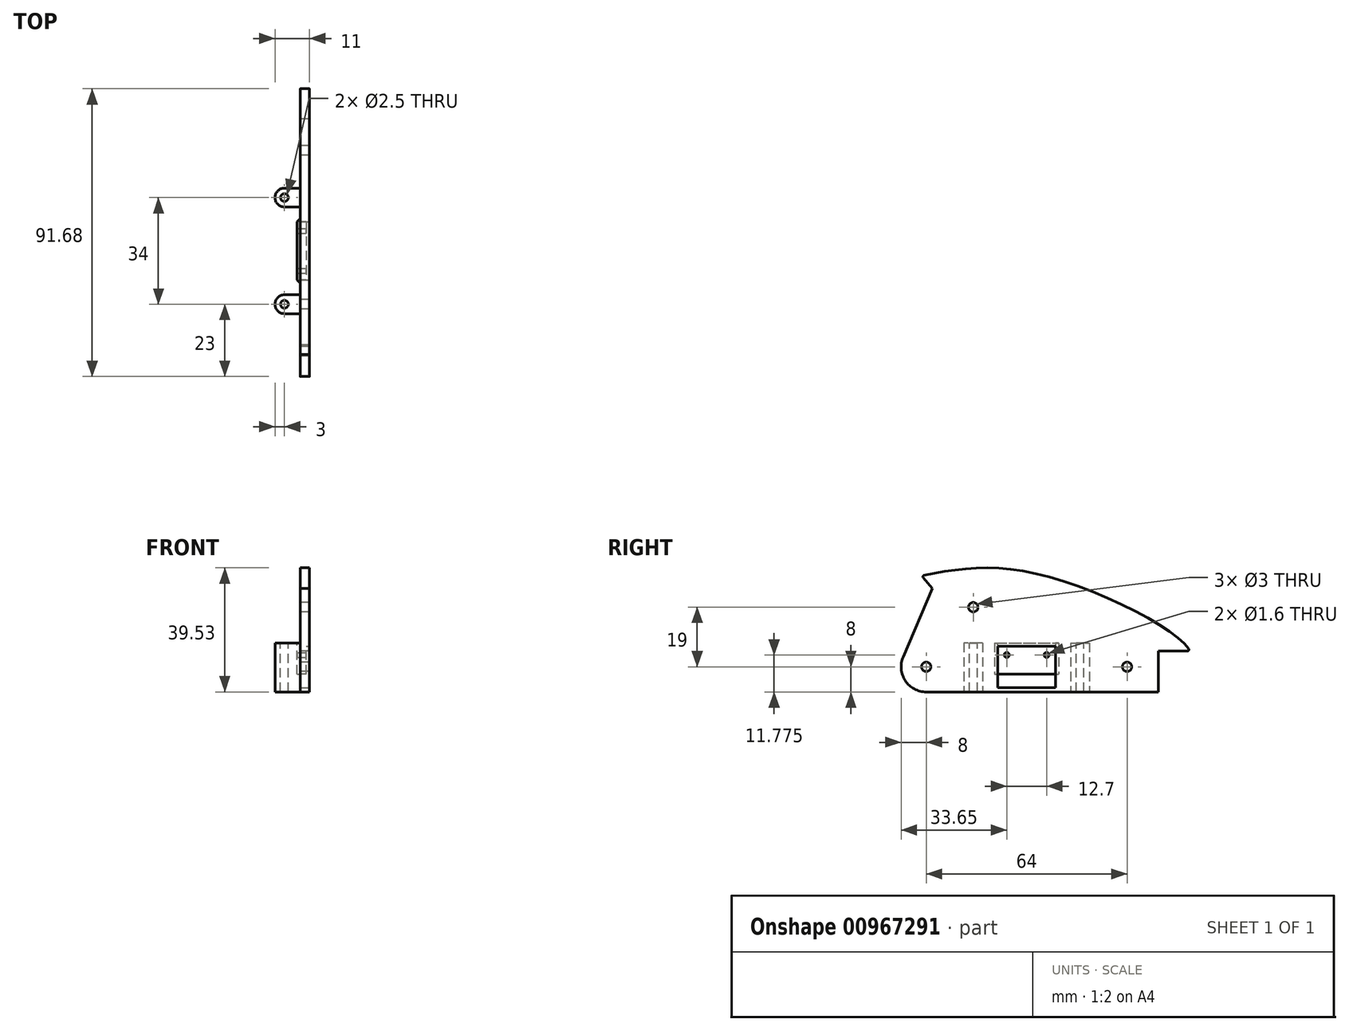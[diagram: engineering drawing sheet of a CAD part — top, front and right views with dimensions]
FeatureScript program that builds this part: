
annotation { "Feature Type Name" : "Feature", "Feature Type Description" : "" }
export const myFeature = defineFeature(function(context is Context, id is Id, definition is map)
    precondition{}
    {
        {
            var Q0;
            Q0=qCreatedBy(makeId("Right.planeOp"),FACE);
            var sketch = newSketch(context, id + "F0", { "sketchPlane" : qUnion([Q0])});
            skCircle(sketch, "E0", {"center": v(0, 0) * mm, "radius": 1.5 * mm});
            skCircle(sketch, "E1", {"center": v(-64, 0) * mm, "radius": 1.5 * mm});
            skCircle(sketch, "E2", {"center": v(-49, 19) * mm, "radius": 1.5 * mm});
            skLineSegment(sketch, "E3", {"start": v(10, -8) * mm, "end": v(-64, -8) * mm});
            skPoint(sketch, "E4", {"position": v(-62, 25) * mm});
            skPoint(sketch, "E5", {"position": v(-65.5, 29) * mm});
            skLineSegment(sketch, "E6", {"start": v(-62, 25) * mm, "end": v(-65.5, 29) * mm});
            skLineSegment(sketch, "E7", {"start": v(10, -8) * mm, "end": v(10, 5) * mm});
            skLineSegment(sketch, "E8", {"start": v(10, 5) * mm, "end": v(20, 5) * mm});
            skFitSpline(sketch, "E9", {"points": [v(-65.5, 29) * mm, v(-25.03, 28.72) * mm, v(20, 5) * mm], "startDerivative": vector(78.35, 16.4) * mm, "endDerivative": vector(13.23, -33.9) * mm});
            skArc(sketch, "E10", {"start": v(-64, -8) * mm, "mid": v(-70.68, -4.4) * mm, "end": v(-71.35, 3.15) * mm});
            skLineSegment(sketch, "E11", {"start": v(-71.35, 3.15) * mm, "end": v(-62, 25) * mm});
            skSolve(sketch);
        }
        {
            var Q0;
            Q0=makeQuery(id+"F0.imprint","IMPRINT",FACE,{"disambiguationData":[TD([[makeQuery(id+"F0.imprint","IMPRINT",EDGE,{"derivedFrom":sQuery(id+"F0.wireOp",EDGE,"E0")}),-1.0]])]});
            extrude(context, id + "F1", {"entities" : qUnion([Q0]), "depth" : 3 * mm, "offsetDistance" : 25 * mm});
        }
        {
            var Q0;
            Q0=makeQuery(id+"F1.opExtrude","CAP_FACE",FACE,{"disambiguationData":[OSD([sQuery(id+"F0.wireOp",EDGE,"E0"),sQuery(id+"F0.wireOp",EDGE,"E1"),sQuery(id+"F0.wireOp",EDGE,"E2"),sQuery(id+"F0.wireOp",EDGE,"E3"),sQuery(id+"F0.wireOp",EDGE,"E6"),sQuery(id+"F0.wireOp",EDGE,"E7"),sQuery(id+"F0.wireOp",EDGE,"E8"),sQuery(id+"F0.wireOp",EDGE,"E9"),sQuery(id+"F0.wireOp",EDGE,"E10"),sQuery(id+"F0.wireOp",EDGE,"E11")])],"isStart":false});
            var sketch = newSketch(context, id + "F2", { "sketchPlane" : qUnion([Q0])});
            skLineSegment(sketch, "E12", {"start": v(-64, 0) * mm, "end": v(0, 0) * mm});
            skLineSegment(sketch, "E13.bottom", {"start": v(-22.75, -6.63) * mm, "end": v(-41.25, -6.63) * mm});
            skLineSegment(sketch, "E13.top", {"start": v(-22.75, 6.62) * mm, "end": v(-41.25, 6.63) * mm});
            skLineSegment(sketch, "E13.left", {"start": v(-22.75, -6.63) * mm, "end": v(-22.75, 6.62) * mm});
            skLineSegment(sketch, "E13.right", {"start": v(-41.25, -6.63) * mm, "end": v(-41.25, 6.63) * mm});
            skPoint(sketch, "E13.middle", {"position": v(-32, 0) * mm});
            skSolve(sketch);
        }
        {
            var Q0;
            {var subQ5=sQuery(id+"F2.wireOp",EDGE,"E13.top");Q0=makeQuery(id+"F2.imprint","IMPRINT",FACE,{"disambiguationData":[TD([[makeQuery(id+"F2.imprint","IMPRINT",EDGE,{"derivedFrom":subQ5}),1.0]])]});}
            var Q1;
            {var subQ5=sQuery(id+"F2.wireOp",EDGE,"E13.bottom");Q1=makeQuery(id+"F2.imprint","IMPRINT",FACE,{"disambiguationData":[TD([[makeQuery(id+"F2.imprint","IMPRINT",EDGE,{"derivedFrom":subQ5}),-1.0]])]});}
            extrude(context, id + "F3", {"entities" : qUnion([Q0, Q1]), "operationType" : NewBodyOperationType.REMOVE, "oppositeDirection" : true, "depth" : 25 * mm, "offsetDistance" : 25 * mm});
        }
        {
            var Q0;
            Q0=makeQuery(id+"F1.opExtrude","CAP_FACE",FACE,{"disambiguationData":[OSD([sQuery(id+"F0.wireOp",EDGE,"E0"),sQuery(id+"F0.wireOp",EDGE,"E1"),sQuery(id+"F0.wireOp",EDGE,"E2"),sQuery(id+"F0.wireOp",EDGE,"E3"),sQuery(id+"F0.wireOp",EDGE,"E6"),sQuery(id+"F0.wireOp",EDGE,"E7"),sQuery(id+"F0.wireOp",EDGE,"E8"),sQuery(id+"F0.wireOp",EDGE,"E9"),sQuery(id+"F0.wireOp",EDGE,"E10"),sQuery(id+"F0.wireOp",EDGE,"E11")])],"isStart":true});
            var sketch = newSketch(context, id + "F4", { "sketchPlane" : qUnion([Q0])});
            skLineSegment(sketch, "E14.bottom", {"start": v(42.25, 7.63) * mm, "end": v(21.75, 7.62) * mm});
            skLineSegment(sketch, "E14.top", {"start": v(42.25, -2.37) * mm, "end": v(21.75, -2.38) * mm});
            skLineSegment(sketch, "E14.left", {"start": v(42.25, 7.63) * mm, "end": v(42.25, -2.37) * mm});
            skLineSegment(sketch, "E14.right", {"start": v(21.75, 7.62) * mm, "end": v(21.75, -2.38) * mm});
            skPoint(sketch, "E14.middle", {"position": v(32, 2.63) * mm});
            skPoint(sketch, "E14.middle.positionSnap0", {"position": v(32, 6.63) * mm});
            skPoint(sketch, "E14.centerSnap0", {"position": v(32, 6.63) * mm});
            skSolve(sketch);
        }
        {
            var Q0;
            {var subQ1=makeQuery(id+"F1.opExtrude","CAP_FACE",FACE,{"disambiguationData":[OSD([sQuery(id+"F0.wireOp",EDGE,"E0"),sQuery(id+"F0.wireOp",EDGE,"E1"),sQuery(id+"F0.wireOp",EDGE,"E2"),sQuery(id+"F0.wireOp",EDGE,"E3"),sQuery(id+"F0.wireOp",EDGE,"E6"),sQuery(id+"F0.wireOp",EDGE,"E7"),sQuery(id+"F0.wireOp",EDGE,"E8"),sQuery(id+"F0.wireOp",EDGE,"E9"),sQuery(id+"F0.wireOp",EDGE,"E10"),sQuery(id+"F0.wireOp",EDGE,"E11")])],"isStart":true});var subQ6=makeQuery(id+"F3.boolean.opBoolean","INTERSECT",EDGE,{"derivedFrom":[subQ1,makeQuery(id+"F3.opExtrude","SWEPT_FACE",FACE,{"disambiguationData":[OSD([sQuery(id+"F2.wireOp",EDGE,"E13.top")])]})]});Q0=makeQuery(id+"F4.imprint","IMPRINT",FACE,{"disambiguationData":[TD([[makeQuery(id+"F4.imprint","IMPRINT",EDGE,{"derivedFrom":subQ6}),-1.0]])]});}
            var Q1;
            Q1=makeQuery(id+"F4.imprint","IMPRINT",FACE,{"disambiguationData":[TD([[makeQuery(id+"F4.imprint","IMPRINT",EDGE,{"derivedFrom":sQuery(id+"F4.wireOp",EDGE,"E14.bottom")}),1.0]])]});
            extrude(context, id + "F5", {"entities" : qUnion([Q0, Q1]), "operationType" : NewBodyOperationType.ADD, "depth" : 1 * mm, "offsetDistance" : 25 * mm});
        }
        {
            var Q0;
            Q0=makeQuery(id+"F5.opExtrude","CAP_FACE",FACE,{"disambiguationData":[OSD([sQuery(id+"F4.wireOp",EDGE,"E14.bottom"),sQuery(id+"F4.wireOp",EDGE,"E14.top"),sQuery(id+"F4.wireOp",EDGE,"E14.left"),sQuery(id+"F4.wireOp",EDGE,"E14.right")])],"isStart":true});
            extrude(context, id + "F6", {"entities" : qUnion([Q0]), "operationType" : NewBodyOperationType.ADD, "depth" : 2 * mm, "offsetDistance" : 25 * mm});
        }
        {
            var Q0;
            Q0=makeQuery(id+"F6.opExtrude","CAP_FACE",FACE,{"disambiguationData":[OSD([sQuery(id+"F4.wireOp",EDGE,"E14.bottom"),sQuery(id+"F4.wireOp",EDGE,"E14.top"),sQuery(id+"F4.wireOp",EDGE,"E14.left"),sQuery(id+"F4.wireOp",EDGE,"E14.right")])],"isStart":false});
            var sketch = newSketch(context, id + "F7", { "sketchPlane" : qUnion([Q0])});
            skPoint(sketch, "E15", {"position": v(-32, 3.78) * mm});
            skPoint(sketch, "E15.positionSnap0", {"position": v(-32, 6.63) * mm});
            skPoint(sketch, "E16", {"position": v(-38.35, 3.78) * mm});
            skPoint(sketch, "E17", {"position": v(-25.65, 3.78) * mm});
            skSolve(sketch);
        }
        {
            var Q0;
            Q0=sQuery(id+"F7.wireOp",VERTEX,"E16");
            var Q1;
            Q1=sQuery(id+"F7.wireOp",VERTEX,"E17");
            var Q2;
            Q2=makeQuery(id+"F1.opExtrude","SWEPT_BODY",BODY,{"disambiguationData":[OSD([sQuery(id+"F0.wireOp",EDGE,"E0"),sQuery(id+"F0.wireOp",EDGE,"E1"),sQuery(id+"F0.wireOp",EDGE,"E2"),sQuery(id+"F0.wireOp",EDGE,"E3"),sQuery(id+"F0.wireOp",EDGE,"E6"),sQuery(id+"F0.wireOp",EDGE,"E7"),sQuery(id+"F0.wireOp",EDGE,"E8"),sQuery(id+"F0.wireOp",EDGE,"E9"),sQuery(id+"F0.wireOp",EDGE,"E10"),sQuery(id+"F0.wireOp",EDGE,"E11")])]});
            hole(context, id + "F8", {"style" : HoleStyle.SIMPLE, "endStyle" : HoleEndStyle.THROUGH, "holeDiameter" : 1.6 * mm, "majorDiameter" : 5 * mm, "tappedDepth" : 12 * mm, "tapClearance" : 3, "startFromSketch" : true, "locations" : qUnion([Q0, Q1]), "scope" : qUnion([Q2])});
        }
        {
            var Q0;
            Q0=makeQuery(id+"F5.opExtrude","CAP_EDGE",EDGE,{"disambiguationData":[OSD([sQuery(id+"F4.wireOp",EDGE,"E14.right")])],"isStart":false});
            var Q1;
            Q1=makeQuery(id+"F5.opExtrude","CAP_EDGE",EDGE,{"disambiguationData":[OSD([sQuery(id+"F4.wireOp",EDGE,"E14.left")])],"isStart":false});
            chamfer(context, id + "F9", {"entities" : qUnion([Q0, Q1]), "width" : 1 * mm, "tangentPropagation" : true});
        }
        {
            var Q0;
            Q0=makeQuery(id+"F1.opExtrude","CAP_FACE",FACE,{"disambiguationData":[OSD([sQuery(id+"F0.wireOp",EDGE,"E0"),sQuery(id+"F0.wireOp",EDGE,"E1"),sQuery(id+"F0.wireOp",EDGE,"E2"),sQuery(id+"F0.wireOp",EDGE,"E3"),sQuery(id+"F0.wireOp",EDGE,"E6"),sQuery(id+"F0.wireOp",EDGE,"E7"),sQuery(id+"F0.wireOp",EDGE,"E8"),sQuery(id+"F0.wireOp",EDGE,"E9"),sQuery(id+"F0.wireOp",EDGE,"E10"),sQuery(id+"F0.wireOp",EDGE,"E11")])],"isStart":true});
            var sketch = newSketch(context, id + "F10", { "sketchPlane" : qUnion([Q0])});
            skPoint(sketch, "E18", {"position": v(49, 19) * mm});
            skLineSegment(sketch, "E19.bottom", {"start": v(46, 7.63) * mm, "end": v(52, 7.63) * mm});
            skLineSegment(sketch, "E19.top", {"start": v(46, 1.63) * mm, "end": v(52, 1.63) * mm});
            skLineSegment(sketch, "E19.left", {"start": v(46, 7.63) * mm, "end": v(46, 1.63) * mm});
            skLineSegment(sketch, "E19.right", {"start": v(52, 7.63) * mm, "end": v(52, 1.63) * mm});
            skPoint(sketch, "E19.middle", {"position": v(49, 4.63) * mm});
            skSolve(sketch);
        }
        {
            var Q0;
            Q0=makeQuery(id+"F10.imprint","IMPRINT",FACE,{"disambiguationData":[TD([[makeQuery(id+"F10.imprint","IMPRINT",EDGE,{"derivedFrom":sQuery(id+"F10.wireOp",EDGE,"E19.bottom")}),-1.0]])]});
            extrude(context, id + "F11", {"entities" : qUnion([Q0]), "operationType" : NewBodyOperationType.ADD, "depth" : 8 * mm, "offsetDistance" : 25 * mm});
        }
        {
            var Q0;
            Q0=makeQuery(id+"F11.opExtrude","CAP_EDGE",EDGE,{"disambiguationData":[OSD([sQuery(id+"F10.wireOp",EDGE,"E19.right")])],"isStart":false});
            var Q1;
            Q1=makeQuery(id+"F11.opExtrude","CAP_EDGE",EDGE,{"disambiguationData":[OSD([sQuery(id+"F10.wireOp",EDGE,"E19.left")])],"isStart":false});
            fillet(context, id + "F12", {"entities" : qUnion([Q0, Q1]), "radius" : 3 * mm, "tangentPropagation" : true, "allowEdgeOverflow" : false});
        }
        {
            var Q0;
            Q0=makeQuery(id+"F1.opExtrude","CAP_FACE",FACE,{"disambiguationData":[OSD([sQuery(id+"F0.wireOp",EDGE,"E0"),sQuery(id+"F0.wireOp",EDGE,"E1"),sQuery(id+"F0.wireOp",EDGE,"E2"),sQuery(id+"F0.wireOp",EDGE,"E3"),sQuery(id+"F0.wireOp",EDGE,"E6"),sQuery(id+"F0.wireOp",EDGE,"E7"),sQuery(id+"F0.wireOp",EDGE,"E8"),sQuery(id+"F0.wireOp",EDGE,"E9"),sQuery(id+"F0.wireOp",EDGE,"E10"),sQuery(id+"F0.wireOp",EDGE,"E11")])],"isStart":true});
            var sketch = newSketch(context, id + "F13", { "sketchPlane" : qUnion([Q0])});
            skLineSegment(sketch, "E20.bottom", {"start": v(18, 7.63) * mm, "end": v(12, 7.63) * mm});
            skLineSegment(sketch, "E20.top", {"start": v(18, 1.63) * mm, "end": v(12, 1.63) * mm});
            skLineSegment(sketch, "E20.left", {"start": v(18, 7.63) * mm, "end": v(18, 1.63) * mm});
            skLineSegment(sketch, "E20.right", {"start": v(12, 7.63) * mm, "end": v(12, 1.63) * mm});
            skSolve(sketch);
        }
        {
            var Q0;
            Q0=makeQuery(id+"F13.imprint","IMPRINT",FACE,{"disambiguationData":[TD([[makeQuery(id+"F13.imprint","IMPRINT",EDGE,{"derivedFrom":sQuery(id+"F13.wireOp",EDGE,"E20.bottom")}),1.0]])]});
            extrude(context, id + "F14", {"entities" : qUnion([Q0]), "operationType" : NewBodyOperationType.ADD, "depth" : 8 * mm, "offsetDistance" : 25 * mm});
        }
        {
            var Q0;
            Q0=makeQuery(id+"F14.opExtrude","CAP_EDGE",EDGE,{"disambiguationData":[OSD([sQuery(id+"F13.wireOp",EDGE,"E20.right")])],"isStart":false});
            var Q1;
            Q1=makeQuery(id+"F14.opExtrude","CAP_EDGE",EDGE,{"disambiguationData":[OSD([sQuery(id+"F13.wireOp",EDGE,"E20.left")])],"isStart":false});
            fillet(context, id + "F15", {"entities" : qUnion([Q0, Q1]), "radius" : 3 * mm, "tangentPropagation" : true, "allowEdgeOverflow" : false});
        }
        {
            var Q0;
            Q0=makeQuery(id+"F11.opExtrude","SWEPT_FACE",FACE,{"disambiguationData":[OSD([sQuery(id+"F10.wireOp",EDGE,"E19.bottom")])]});
            var sketch = newSketch(context, id + "F16", { "sketchPlane" : qUnion([Q0])});
            skPoint(sketch, "E21", {"position": v(-5, -49) * mm});
            skArc(sketch, "E22.0", {"start": v(-5, -12) * mm, "mid": v(-8, -15) * mm, "end": v(-5, -18) * mm});
            skSolve(sketch);
        }
        {
            var Q0;
            Q0=sQuery(id+"F16.wireOp",VERTEX,"E21");
            var Q1;
            Q1=sQuery(id+"F16.wireOp",VERTEX,"E22.0.center");
            var Q2;
            Q2=makeQuery(id+"F1.opExtrude","SWEPT_BODY",BODY,{"disambiguationData":[OSD([sQuery(id+"F0.wireOp",EDGE,"E0"),sQuery(id+"F0.wireOp",EDGE,"E1"),sQuery(id+"F0.wireOp",EDGE,"E2"),sQuery(id+"F0.wireOp",EDGE,"E3"),sQuery(id+"F0.wireOp",EDGE,"E6"),sQuery(id+"F0.wireOp",EDGE,"E7"),sQuery(id+"F0.wireOp",EDGE,"E8"),sQuery(id+"F0.wireOp",EDGE,"E9"),sQuery(id+"F0.wireOp",EDGE,"E10"),sQuery(id+"F0.wireOp",EDGE,"E11")])]});
            hole(context, id + "F17", {"style" : HoleStyle.SIMPLE, "endStyle" : HoleEndStyle.THROUGH, "holeDiameter" : 2.5 * mm, "majorDiameter" : 5 * mm, "tappedDepth" : 12 * mm, "tapClearance" : 3, "startFromSketch" : true, "locations" : qUnion([Q0, Q1]), "scope" : qUnion([Q2])});
        }
        {
            var Q0;
            Q0=makeQuery(id+"F1.opExtrude","SWEPT_EDGE",EDGE,{"disambiguationData":[OSD([sQuery(id+"F0.wireOp",EDGE,"E6"),sQuery(id+"F0.wireOp",EDGE,"E9")])]});
            var Q1;
            Q1=makeQuery(id+"F1.opExtrude","SWEPT_EDGE",EDGE,{"disambiguationData":[OSD([sQuery(id+"F0.wireOp",EDGE,"E8"),sQuery(id+"F0.wireOp",EDGE,"E9")])]});
            fillet(context, id + "F18", {"entities" : qUnion([Q0, Q1]), "radius" : 0.5 * mm, "tangentPropagation" : true, "allowEdgeOverflow" : false});
        }
        {
            var Q0;
            Q0=makeQuery(id+"F14.opExtrude","SWEPT_FACE",FACE,{"disambiguationData":[OSD([sQuery(id+"F13.wireOp",EDGE,"E20.top")])]});
            var Q1;
            Q1=makeQuery(id+"F11.opExtrude","SWEPT_FACE",FACE,{"disambiguationData":[OSD([sQuery(id+"F10.wireOp",EDGE,"E19.top")])]});
            extrude(context, id + "F19", {"entities" : qUnion([Q0, Q1]), "operationType" : NewBodyOperationType.ADD, "depth" : 9.62 * mm, "offsetDistance" : 25 * mm});
        }
    });
